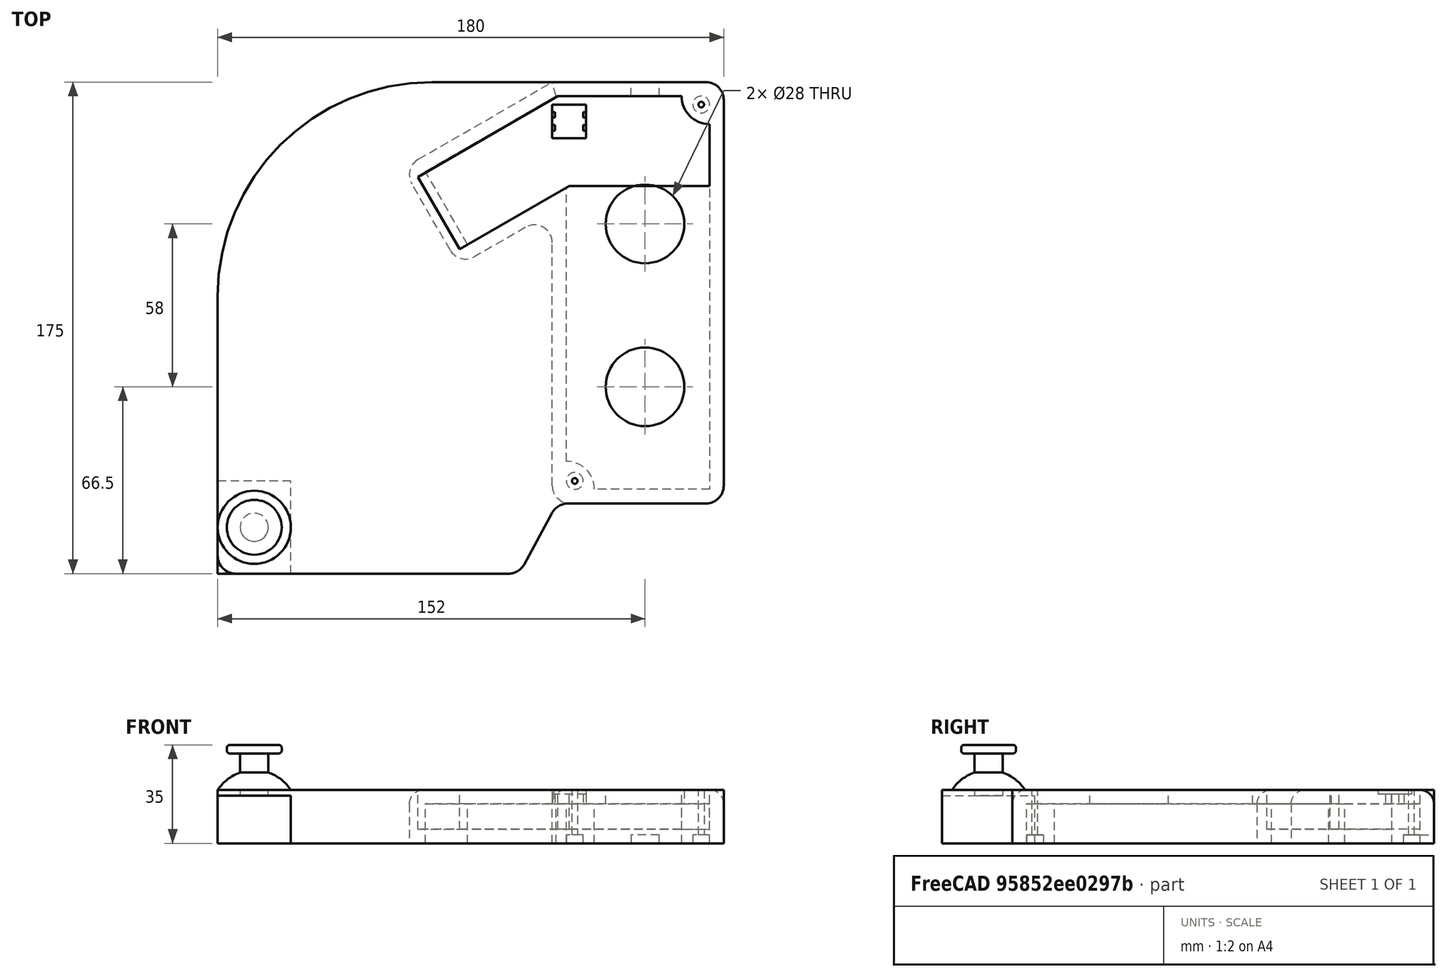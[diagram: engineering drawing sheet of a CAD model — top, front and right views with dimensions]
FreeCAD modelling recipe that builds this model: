
FCSTD DOCUMENT  (FreeCAD 0.19R21125 (Git))
Label: base1
Comment: HyperController Enclosure Prototype
License: GPLv3
LicenseURL: https://www.gnu.org/licenses/gpl-3.0.en.html
objects: Sketcher::SketchObject×17, PartDesign::CoordinateSystem×9, PartDesign::Pocket×8, PartDesign::Pad×5, App::Link×5, PartDesign::Fillet×4, PartDesign::Body×3, App::DocumentObjectGroup×2, App::FeaturePython×2, App::Part×2, PartDesign::Revolution×1, Mesh::Feature×1
note: 65 computed .brp shape members not serialized (recipe doc carries the construction recipe); baked Part::Feature solids carry a one-line shape summary decoded from their .brp

FEATURE [Sketcher::SketchObject] Sketch  label="Base_Ref"
  MapMode = 5
  Support = -> [XY_Plane]
  expr: Constraints[9] = vars.base_l
  expr: Constraints[10] = vars.base_w
  sketch-geometry (4):
    g0: LineSegment StartX=0 StartY=175 StartZ=0 EndX=180 EndY=175 EndZ=0
    g1: LineSegment StartX=180 StartY=175 StartZ=0 EndX=180 EndY=0 EndZ=0
    g2: LineSegment StartX=180 StartY=0 StartZ=0 EndX=0 EndY=0 EndZ=0
    g3: LineSegment StartX=0 StartY=0 StartZ=0 EndX=0 EndY=175 EndZ=0
  constraints (11):
    c: Coincident(g0,g1)
    c: Coincident(g1,g2)
    c: Coincident(g2,g3)
    c: Coincident(g3,g0)
    c: Horizontal(g0)
    c: Horizontal(g2)
    c: Vertical(g1)
    c: Vertical(g3)
    c: Coincident(g2,g-1)
    c: DistanceY(g1,g1) = 175
    c: DistanceX(g0,g0) = 180
FEATURE [Sketcher::SketchObject] Sketch001  label="Base"
  ExternalGeometry = -> [Sketch]
  MapMode = 5
  Support = -> [XY_Plane]
  expr: Constraints[6] = vars.round
  expr: Constraints[10] = vars.round
  expr: Constraints[17] = vars.big_round
  expr: Constraints[22] = vars.round
  expr: Constraints[23] = vars.round
  expr: Constraints[24] = vars.joystick1_margin_out - vars.joystick1_margin_in
  expr: Constraints[25] = vars.joystick1_margin_right + vars.joystick_w + vars.joystick1_margin_left
  sketch-geometry (11):
    g0: LineSegment StartX=180 StartY=175 StartZ=0 EndX=180 EndY=31.35 EndZ=0
    g1: LineSegment StartX=173.65 StartY=25 StartZ=0 EndX=124.577 EndY=25 EndZ=0
    g2: LineSegment StartX=119 StartY=21.6858 StartZ=0 EndX=109 EndY=3.31418 EndZ=0
    g3: LineSegment StartX=103.423 StartY=0 StartZ=0 EndX=6.35 EndY=0 EndZ=0
    g4: ArcOfCircle CenterX=124.577 CenterY=18.65 CenterZ=0 NormalX=0 NormalY=0 NormalZ=1 AngleXU=0 Radius=6.35 StartAngle=1.5708 EndAngle=2.64312
    g5: ArcOfCircle CenterX=103.423 CenterY=6.35 CenterZ=0 NormalX=0 NormalY=0 NormalZ=1 AngleXU=0 Radius=6.35 StartAngle=4.71239 EndAngle=5.78472
    g6: LineSegment StartX=180 StartY=175 StartZ=0 EndX=76.2 EndY=175 EndZ=0
    g7: LineSegment StartX=0 StartY=98.8 StartZ=0 EndX=0 EndY=6.35 EndZ=0
    g8: ArcOfCircle CenterX=76.2 CenterY=98.8 CenterZ=0 NormalX=0 NormalY=0 NormalZ=1 AngleXU=0 Radius=76.2 StartAngle=1.5708 EndAngle=3.14159
    g9: ArcOfCircle CenterX=173.65 CenterY=31.35 CenterZ=0 NormalX=0 NormalY=0 NormalZ=1 AngleXU=0 Radius=6.35 StartAngle=4.71239 EndAngle=6.28319
    g10: ArcOfCircle CenterX=6.35 CenterY=6.35 CenterZ=0 NormalX=0 NormalY=0 NormalZ=1 AngleXU=0 Radius=6.35 StartAngle=3.14159 EndAngle=4.71239
  constraints (27):
    c: Coincident(g-3,g0)
    c: Vertical(g0)
    c: Horizontal(g1)
    c: PointOnObject(g3,g-5)
    c: Tangent(g4,g1) = -1.5708
    c: Tangent(g4,g2) = -1.5708
    c: Radius(g4) = 6.35
    c: PointOnObject(g3,g-5)
    c: Tangent(g5,g2) = 1.5708
    c: Tangent(g5,g3) = 1.5708
    c: Radius(g5) = 6.35
    c: Coincident(g6,g0)
    c: Horizontal(g6)
    c: PointOnObject(g7,g-4)
    c: PointOnObject(g7,g-4)
    c: Tangent(g8,g6) = -1.5708
    c: Tangent(g8,g7) = -1.5708
    c: Radius(g8) = 76.2
    c: Tangent(g9,g0) = 1.5708
    c: Tangent(g9,g1) = 1.5708
    c: Tangent(g10,g3) = 1.5708
    c: Tangent(g10,g7) = -1.5708
    c: Radius(g10) = 6.35
    c: Radius(g9) = 6.35
    c: DistanceY(g-5,g1) = 25
    c: DistanceX(g2,g0) = 61
    c: DistanceX(g2,g2) = 10
FEATURE [PartDesign::Pad] Pad
  Length = 19
  Length2 = 100
  Profile = -> Sketch001
  Type = 0
  expr: Length = vars.base_t
FEATURE [Sketcher::SketchObject] Sketch002  label="Base_Ref001"
  MapMode = 5
  Support = -> [XY_Plane001]
  expr: Constraints[10] = vars.base_w
  expr: Constraints[9] = vars.base_l
  sketch-geometry (4):
    g0: LineSegment StartX=0 StartY=175 StartZ=0 EndX=180 EndY=175 EndZ=0
    g1: LineSegment StartX=180 StartY=175 StartZ=0 EndX=180 EndY=0 EndZ=0
    g2: LineSegment StartX=180 StartY=0 StartZ=0 EndX=0 EndY=0 EndZ=0
    g3: LineSegment StartX=0 StartY=0 StartZ=0 EndX=0 EndY=175 EndZ=0
  constraints (11):
    c: Coincident(g0,g1)
    c: Coincident(g1,g2)
    c: Coincident(g2,g3)
    c: Coincident(g3,g0)
    c: Horizontal(g0)
    c: Horizontal(g2)
    c: Vertical(g1)
    c: Vertical(g3)
    c: Coincident(g2,g-1)
    c: DistanceY(g1,g1) = 175
    c: DistanceX(g0,g0) = 180
FEATURE [Sketcher::SketchObject] Sketch003  label="Base001"
  ExternalGeometry = -> [Sketch002]
  MapMode = 5
  Support = -> [XY_Plane001]
  expr: Constraints[25] = vars.joystick1_margin_right + vars.joystick_w + vars.joystick1_margin_left
  expr: Constraints[24] = vars.joystick1_margin_out - vars.joystick1_margin_in
  expr: Constraints[23] = vars.round
  expr: Constraints[22] = vars.round
  expr: Constraints[17] = vars.big_round
  expr: Constraints[10] = vars.round
  expr: Constraints[6] = vars.round
  sketch-geometry (11):
    g0: LineSegment StartX=180 StartY=175 StartZ=0 EndX=180 EndY=31.35 EndZ=0
    g1: LineSegment StartX=173.65 StartY=25 StartZ=0 EndX=124.577 EndY=25 EndZ=0
    g2: LineSegment StartX=119 StartY=21.6858 StartZ=0 EndX=109 EndY=3.31418 EndZ=0
    g3: LineSegment StartX=103.423 StartY=0 StartZ=0 EndX=6.35 EndY=0 EndZ=0
    g4: ArcOfCircle CenterX=124.577 CenterY=18.65 CenterZ=0 NormalX=0 NormalY=0 NormalZ=1 AngleXU=0 Radius=6.35 StartAngle=1.5708 EndAngle=2.64312
    g5: ArcOfCircle CenterX=103.423 CenterY=6.35 CenterZ=0 NormalX=0 NormalY=0 NormalZ=1 AngleXU=0 Radius=6.35 StartAngle=4.71239 EndAngle=5.78472
    g6: LineSegment StartX=180 StartY=175 StartZ=0 EndX=76.2 EndY=175 EndZ=0
    g7: LineSegment StartX=0 StartY=98.8 StartZ=0 EndX=0 EndY=6.35 EndZ=0
    g8: ArcOfCircle CenterX=76.2 CenterY=98.8 CenterZ=0 NormalX=0 NormalY=0 NormalZ=1 AngleXU=0 Radius=76.2 StartAngle=1.5708 EndAngle=3.14159
    g9: ArcOfCircle CenterX=173.65 CenterY=31.35 CenterZ=0 NormalX=0 NormalY=0 NormalZ=1 AngleXU=0 Radius=6.35 StartAngle=4.71239 EndAngle=6.28319
    g10: ArcOfCircle CenterX=6.35 CenterY=6.35 CenterZ=0 NormalX=0 NormalY=0 NormalZ=1 AngleXU=0 Radius=6.35 StartAngle=3.14159 EndAngle=4.71239
  constraints (27):
    c: Coincident(g-3,g0)
    c: Vertical(g0)
    c: Horizontal(g1)
    c: PointOnObject(g3,g-5)
    c: Tangent(g4,g1) = -1.5708
    c: Tangent(g4,g2) = -1.5708
    c: Radius(g4) = 6.35
    c: PointOnObject(g3,g-5)
    c: Tangent(g5,g2) = 1.5708
    c: Tangent(g5,g3) = 1.5708
    c: Radius(g5) = 6.35
    c: Coincident(g6,g0)
    c: Horizontal(g6)
    c: PointOnObject(g7,g-4)
    c: PointOnObject(g7,g-4)
    c: Tangent(g8,g6) = -1.5708
    c: Tangent(g8,g7) = -1.5708
    c: Radius(g8) = 76.2
    c: Tangent(g9,g0) = 1.5708
    c: Tangent(g9,g1) = 1.5708
    c: Tangent(g10,g3) = 1.5708
    c: Tangent(g10,g7) = -1.5708
    c: Radius(g10) = 6.35
    c: Radius(g9) = 6.35
    c: DistanceY(g-5,g1) = 25
    c: DistanceX(g2,g0) = 61
    c: DistanceX(g2,g2) = 10
FEATURE [Sketcher::SketchObject] Sketch004
  ExternalGeometry = -> [Sketch002]
  MapMode = 5
  Support = -> [XY_Plane001]
  expr: Constraints[18] = vars.joystick_sep
  expr: Constraints[19] = vars.joystick1_margin_right
  expr: Constraints[23] = vars.joystick_w
  expr: Constraints[20] = vars.joystick1_margin_out
  expr: Constraints[22] = vars.joystick_l
  expr: Constraints[25] = vars.joystick_w / 2 + 1
  sketch-geometry (11):
    g0: LineSegment [constr] StartX=139 StartY=83 StartZ=0 EndX=165 EndY=83 EndZ=0
    g1: LineSegment [constr] StartX=165 StartY=83 StartZ=0 EndX=165 EndY=50 EndZ=0
    g2: LineSegment [constr] StartX=165 StartY=50 StartZ=0 EndX=139 EndY=50 EndZ=0
    g3: LineSegment [constr] StartX=139 StartY=50 StartZ=0 EndX=139 EndY=83 EndZ=0
    g4: LineSegment [constr] StartX=139 StartY=141 StartZ=0 EndX=165 EndY=141 EndZ=0
    g5: LineSegment [constr] StartX=165 StartY=141 StartZ=0 EndX=165 EndY=108 EndZ=0
    g6: LineSegment [constr] StartX=165 StartY=108 StartZ=0 EndX=139 EndY=108 EndZ=0
    g7: LineSegment [constr] StartX=139 StartY=108 StartZ=0 EndX=139 EndY=141 EndZ=0
    g8: Circle CenterX=152 CenterY=124.5 CenterZ=0 NormalX=0 NormalY=0 NormalZ=1 AngleXU=0 Radius=14
    g9: GeomPoint X=152 Y=66.5 Z=0
    g10: Circle CenterX=152 CenterY=66.5 CenterZ=0 NormalX=0 NormalY=0 NormalZ=1 AngleXU=0 Radius=14
  constraints (29):
    c: Coincident(g0,g1)
    c: Coincident(g1,g2)
    c: Coincident(g2,g3)
    c: Coincident(g3,g0)
    c: Horizontal(g0)
    c: Horizontal(g2)
    c: Vertical(g1)
    c: Vertical(g3)
    c: Coincident(g4,g5)
    c: Coincident(g5,g6)
    c: Coincident(g6,g7)
    c: Coincident(g7,g4)
    c: Horizontal(g4)
    c: Horizontal(g6)
    c: Vertical(g5)
    c: Vertical(g7)
    c: PointOnObject(g6,g3)
    c: PointOnObject(g5,g1)
    c: DistanceY(g0,g5) = 25
    c: DistanceX(g1,g-3) = 15
    c: DistanceY(g-3,g1) = 50
    c: Equal(g5,g1)
    c: DistanceY(g1,g1) = 33
    c: DistanceX(g4,g4) = 26
    c: Symmetric(g5,g4,g8)
    c: Radius(g8) = 14
    c: Symmetric(g0,g1,g9)
    c: Coincident(g10,g9)
    c: Equal(g10,g8)
FEATURE [PartDesign::CoordinateSystem] LCS_Origin
  AttacherType = Attacher::AttachEngine3D
  MapMode = 2
  Support = -> [X_Axis002]
FEATURE [App::DocumentObjectGroup] Constraints
FEATURE [App::FeaturePython] Variables  # WARN: FeaturePython — macro-defined, semantics opaque (R4)
FEATURE [App::Link] BasePlate  label="BasePlate001"
  LinkedObject = -> Body
FEATURE [PartDesign::CoordinateSystem] LCS_1
  AttacherType = Attacher::AttachEngine3D
  MapMode = 7
  Placement = pos=(180,0,0) rot=(0,0.707107,0.707107;3.14159rad)
  Support = -> [Sketch]
FEATURE [PartDesign::CoordinateSystem] LCS_2
  AttacherType = Attacher::AttachEngine3D
  MapMode = 7
  Placement = pos=(180,0,0) rot=(0,0.707107,0.707107;3.14159rad)
  Support = -> [Sketch002]
FEATURE [App::Link] TopPlate  label="TopPlate001"
  AssemblyType = Asm4EE
  AttachedBy = #LCS_2
  AttachedTo = BasePlate#LCS_1
  AttachmentOffset = pos=(0,19,0) rot=(0,0,1;0rad)
  LinkPlacement = pos=(0,-3.6e-15,19) rot=(0,0,1;0rad)
  LinkedObject = -> Body001
  Placement = pos=(0,-3.6e-15,19) rot=(0,0,1;0rad)
  expr: Placement = BasePlate.Placement * LCS_1.Placement * AttachmentOffset * LCS_2.Placement ^ -1
  expr: .AttachmentOffset.Base.y = vars.base_t
FEATURE [Sketcher::SketchObject] Sketch005
  ExternalGeometry = -> [Sketch002]
  MapMode = 5
  Support = -> [XY_Plane001]
  expr: Constraints[56] = vars.buttons_l
  expr: Constraints[46] = vars.buttons_angle
  expr: Constraints[32] = vars.joystick1_margin_out - vars.joystick1_margin_in
  expr: Constraints[28] = vars.round
  expr: Constraints[55] = vars.buttons_w
  expr: Constraints[22] = vars.joystick_l
  expr: Constraints[20] = vars.joystick1_margin_out
  expr: Constraints[23] = vars.joystick_w
  expr: Constraints[19] = vars.joystick1_margin_right
  expr: Constraints[36] = vars.joystick1_margin_left
  expr: Constraints[18] = vars.joystick_sep
  sketch-geometry (21):
    g0: LineSegment [constr] StartX=139 StartY=83 StartZ=0 EndX=165 EndY=83 EndZ=0
    g1: LineSegment [constr] StartX=165 StartY=83 StartZ=0 EndX=165 EndY=50 EndZ=0
    g2: LineSegment [constr] StartX=165 StartY=50 StartZ=0 EndX=139 EndY=50 EndZ=0
    g3: LineSegment [constr] StartX=139 StartY=50 StartZ=0 EndX=139 EndY=83 EndZ=0
    g4: LineSegment [constr] StartX=139 StartY=141 StartZ=0 EndX=165 EndY=141 EndZ=0
    g5: LineSegment [constr] StartX=165 StartY=141 StartZ=0 EndX=165 EndY=108 EndZ=0
    g6: LineSegment [constr] StartX=165 StartY=108 StartZ=0 EndX=139 EndY=108 EndZ=0
    g7: LineSegment [constr] StartX=139 StartY=108 StartZ=0 EndX=139 EndY=141 EndZ=0
    g8: LineSegment StartX=119 StartY=31.35 StartZ=0 EndX=119 EndY=117.813 EndZ=0
    g9: LineSegment StartX=109.475 StartY=123.313 StartZ=0 EndX=91.3686 EndY=112.859 EndZ=0
    g10: LineSegment StartX=82.6943 StartY=115.183 StartZ=0 EndX=69.0443 EndY=138.826 EndZ=0
    g11: LineSegment StartX=71.3686 StartY=147.5 StartZ=0 EndX=119 EndY=175 EndZ=0
    g12: LineSegment StartX=119 StartY=175 StartZ=0 EndX=173.65 EndY=175 EndZ=0
    g13: LineSegment StartX=180 StartY=168.65 StartZ=0 EndX=180 EndY=31.35 EndZ=0
    g14: LineSegment StartX=173.65 StartY=25 StartZ=0 EndX=125.35 EndY=25 EndZ=0
    g15: ArcOfCircle CenterX=173.65 CenterY=31.35 CenterZ=0 NormalX=0 NormalY=0 NormalZ=1 AngleXU=0 Radius=6.35 StartAngle=4.71239 EndAngle=6.28319
    g16: ArcOfCircle CenterX=125.35 CenterY=31.35 CenterZ=0 NormalX=0 NormalY=0 NormalZ=1 AngleXU=0 Radius=6.35 StartAngle=3.14159 EndAngle=4.71239
    g17: ArcOfCircle CenterX=112.65 CenterY=117.813 CenterZ=0 NormalX=0 NormalY=0 NormalZ=1 AngleXU=0 Radius=6.35 StartAngle=7e-16 EndAngle=2.0944
    g18: ArcOfCircle CenterX=88.1936 CenterY=118.358 CenterZ=0 NormalX=0 NormalY=0 NormalZ=1 AngleXU=0 Radius=6.35 StartAngle=3.66519 EndAngle=5.23599
    g19: ArcOfCircle CenterX=74.5436 CenterY=142.001 CenterZ=0 NormalX=0 NormalY=0 NormalZ=1 AngleXU=0 Radius=6.35 StartAngle=2.0944 EndAngle=3.66519
    g20: ArcOfCircle CenterX=173.65 CenterY=168.65 CenterZ=0 NormalX=0 NormalY=0 NormalZ=1 AngleXU=0 Radius=6.35 StartAngle=3e-16 EndAngle=1.5708
  constraints (57):
    c: Coincident(g0,g1)
    c: Coincident(g1,g2)
    c: Coincident(g2,g3)
    c: Coincident(g3,g0)
    c: Horizontal(g0)
    c: Horizontal(g2)
    c: Vertical(g1)
    c: Vertical(g3)
    c: Coincident(g4,g5)
    c: Coincident(g5,g6)
    c: Coincident(g6,g7)
    c: Coincident(g7,g4)
    c: Horizontal(g4)
    c: Horizontal(g6)
    c: Vertical(g5)
    c: Vertical(g7)
    c: PointOnObject(g6,g3)
    c: PointOnObject(g5,g1)
    c: DistanceY(g0,g5) = 25
    c: DistanceX(g1,g-3) = 15
    c: DistanceY(g-3,g1) = 50
    c: Equal(g5,g1)
    c: DistanceY(g1,g1) = 33
    c: DistanceX(g4,g4) = 26
    c: Vertical(g8)
    c: Horizontal(g12)
    c: Tangent(g15,g13) = 1.5708
    c: Tangent(g15,g14) = 1.5708
    c: Radius(g15) = 6.35
    c: Horizontal(g14)
    c: Vertical(g13)
    c: PointOnObject(g-3,g13)
    c: DistanceY(g-3,g14) = 25
    c: Tangent(g16,g14) = 1.5708
    c: Tangent(g16,g8) = 1.5708
    c: Equal(g16,g15)
    c: DistanceX(g8,g2) = 20
    c: Tangent(g17,g8) = -1.5708
    c: Tangent(g17,g9) = -1.5708
    c: Tangent(g19,g11) = 1.5708
    c: Tangent(g18,g9) = 1.5708
    c: Tangent(g18,g10) = 1.5708
    c: Equal(g16,g17)
    c: Equal(g17,g18)
    c: Equal(g18,g19)
    c: Parallel(g11,g9)
    c: Angle(g9,g8) = 1.0472
    c: Perpendicular(g9,g10)
    c: Tangent(g20,g13) = 1.5708
    c: Tangent(g20,g12) = 1.5708
    c: Equal(g16,g20)
    c: Coincident(g11,g12)
    c: PointOnObject(g11,g8)
    c: PointOnObject(g11,g-4)
    c: Tangent(g10,g19) = 1.5708
    c: Distance(g9,g11) = 40
    c: Distance(g11) = 55
FEATURE [PartDesign::Pad] Pad001
  Length = 19
  Length2 = 100
  Profile = -> Sketch005
  Type = 0
  expr: Length = vars.base_t
FEATURE [PartDesign::Pocket] Pocket
  BaseFeature = -> Pad001
  Length = 5
  Length2 = 100
  Midplane = true
  Profile = -> Sketch004
  Type = 1
FEATURE [Sketcher::SketchObject] Sketch006
  ExternalGeometry = -> [Sketch005]
  MapMode = 5
  Support = -> [XY_Plane001]
  expr: Constraints[11] = vars.top_wall
  expr: Constraints[16] = vars.buttons_w - 2 * vars.top_wall
  expr: Constraints[12] = vars.top_wall
  expr: Constraints[10] = vars.top_wall
  expr: Constraints[32] = vars.top_wall
  sketch-geometry (11):
    g0: LineSegment StartX=73.8686 StartY=143.17 StartZ=0 EndX=120.34 EndY=170 EndZ=0
    g1: LineSegment StartX=120.34 StartY=170 StartZ=0 EndX=165 EndY=170 EndZ=0
    g2: LineSegment StartX=175 StartY=160 StartZ=0 EndX=175 EndY=30 EndZ=0
    g3: LineSegment StartX=175 StartY=30 StartZ=0 EndX=134 EndY=30 EndZ=0
    g4: LineSegment StartX=124 StartY=40 StartZ=0 EndX=124 EndY=137.472 EndZ=0
    g5: LineSegment StartX=124 StartY=137.472 StartZ=0 EndX=88.8686 EndY=117.189 EndZ=0
    g6: LineSegment StartX=88.8686 StartY=117.189 StartZ=0 EndX=73.8686 EndY=143.17 EndZ=0
    g7: LineSegment [constr] StartX=71.3686 StartY=147.5 StartZ=0 EndX=73.8686 EndY=143.17 EndZ=0
    g8: LineSegment [constr] StartX=88.8686 StartY=117.189 StartZ=0 EndX=91.3686 EndY=112.859 EndZ=0
    g9: ArcOfCircle CenterX=175 CenterY=170 CenterZ=0 NormalX=0 NormalY=0 NormalZ=1 AngleXU=0 Radius=10 StartAngle=3.14159 EndAngle=4.71239
    g10: ArcOfCircle CenterX=124 CenterY=30 CenterZ=0 NormalX=0 NormalY=0 NormalZ=1 AngleXU=0 Radius=10 StartAngle=-9e-16 EndAngle=1.5708
  constraints (33):
    c: Coincident(g0,g1)
    c: Horizontal(g1)
    c: Vertical(g2)
    c: Coincident(g2,g3)
    c: Vertical(g4)
    c: Coincident(g4,g5)
    c: Coincident(g5,g6)
    c: Parallel(g-3,g3)
    c: Parallel(g5,g-8)
    c: Parallel(g6,g-9)
    c: DistanceY(g-3,g2) = 5
    c: DistanceX(g2,g-5) = 5
    c: DistanceY(g1,g-6) = 5
    c: Coincident(g0,g6)
    c: Parallel(g0,g-7)
    c: PointOnObject(g-7,g6)
    c: Distance(g6) = 30
    c: Coincident(g7,g-7)
    c: Coincident(g7,g0)
    c: Coincident(g8,g5)
    c: Coincident(g8,g-8)
    c: Equal(g8,g7)
    c: Coincident(g9,g1)
    c: Coincident(g9,g2)
    c: Radius(g9) = 10
    c: PointOnObject(g9,g1)
    c: PointOnObject(g9,g2)
    c: Coincident(g10,g4)
    c: Coincident(g10,g3)
    c: Equal(g9,g10)
    c: PointOnObject(g10,g4)
    c: PointOnObject(g10,g3)
    c: DistanceX(g-4,g10) = 5
FEATURE [PartDesign::Pocket] Pocket001
  BaseFeature = -> Pocket
  Length = 14
  Length2 = 100
  Profile = -> Sketch006
  Reversed = true
  Type = 0
  expr: Length = vars.base_t - vars.top_wall
FEATURE [PartDesign::Fillet] Fillet001
  Base = -> Pad [Edge1]
  BaseFeature = -> Pad
  Radius = 6.35
  SupportTransform = true
  expr: Radius = vars.round
FEATURE [Sketcher::SketchObject] Sketch007
  AttachmentOffset = pos=(0,0,5) rot=(0,0,1;0rad)
  ExternalGeometry = -> [Sketch]
  MapMode = 5
  Placement = pos=(0,0,5) rot=(0,0,1;0rad)
  Support = -> [XY_Plane]
  expr: Constraints[12] = vars.top_wall
  expr: .AttachmentOffset.Base.z = vars.top_wall
  expr: Constraints[11] = vars.top_wall
  expr: Constraints[5] = 22
  expr: Constraints[19] = vars.buttons_angle + 90
  expr: Constraints[20] = 45
  sketch-geometry (7):
    g0: LineSegment StartX=165 StartY=170 StartZ=0 EndX=121 EndY=170 EndZ=0
    g1: LineSegment StartX=125 StartY=138 StartZ=0 EndX=175 EndY=138 EndZ=0
    g2: LineSegment StartX=175 StartY=138 StartZ=0 EndX=175 EndY=160 EndZ=0
    g3: ArcOfCircle CenterX=175 CenterY=170 CenterZ=0 NormalX=0 NormalY=0 NormalZ=1 AngleXU=0 Radius=10 StartAngle=3.14159 EndAngle=4.71239
    g4: LineSegment StartX=121 StartY=170 StartZ=0 EndX=71.1725 EndY=141.232 EndZ=0
    g5: LineSegment StartX=71.1725 StartY=141.232 StartZ=0 EndX=86.0289 EndY=115.5 EndZ=0
    g6: LineSegment StartX=86.0289 StartY=115.5 StartZ=0 EndX=125 EndY=138 EndZ=0
  constraints (22):
    c: Coincident(g1,g2)
    c: Horizontal(g0)
    c: Horizontal(g1)
    c: Vertical(g2)
    c: DistanceX(g1,g1) = 50
    c: DistanceY(g2,g2) = 22
    c: Coincident(g3,g0)
    c: Coincident(g3,g2)
    c: PointOnObject(g3,g0)
    c: PointOnObject(g3,g2)
    c: Radius(g3) = 10
    c: DistanceX(g2,g-3) = 5
    c: DistanceY(g0,g-3) = 5
    c: Coincident(g0,g4)
    c: Coincident(g4,g5)
    c: Coincident(g5,g6)
    c: Coincident(g6,g1)
    c: Parallel(g6,g4)
    c: Perpendicular(g5,g4)
    c: Angle(g4,g0) = 2.61799
    c: Distance(g6) = 45
    c: DistanceX(g0,g0) = 44
FEATURE [PartDesign::Pocket] Pocket002
  BaseFeature = -> Fillet001
  Length = 5
  Length2 = 100
  Profile = -> Sketch007
  Reversed = true
  Type = 1
FEATURE [Sketcher::SketchObject] Sketch008
  MapMode = 5
  Support = -> [XY_Plane003]
  expr: Constraints[9] = vars.joystick_l
  expr: Constraints[10] = vars.joystick_w
  sketch-geometry (4):
    g0: LineSegment StartX=0 StartY=0 StartZ=0 EndX=26 EndY=0 EndZ=0
    g1: LineSegment StartX=26 StartY=0 StartZ=0 EndX=26 EndY=33 EndZ=0
    g2: LineSegment StartX=26 StartY=33 StartZ=0 EndX=0 EndY=33 EndZ=0
    g3: LineSegment StartX=0 StartY=33 StartZ=0 EndX=0 EndY=0 EndZ=0
  constraints (11):
    c: Coincident(g0,g1)
    c: Coincident(g1,g2)
    c: Coincident(g2,g3)
    c: Coincident(g3,g0)
    c: Horizontal(g0)
    c: Horizontal(g2)
    c: Vertical(g1)
    c: Vertical(g3)
    c: Coincident(g0,g-1)
    c: DistanceY(g1,g1) = 33
    c: DistanceX(g0,g0) = 26
FEATURE [PartDesign::Pad] Pad002
  Length = 17
  Length2 = 100
  Profile = -> Sketch008
  Type = 0
  expr: Length = vars.joystick_h1
FEATURE [Sketcher::SketchObject] Sketch009
  MapMode = 5
  Support = -> [XY_Plane003]
  expr: Constraints[0] = vars.joystick_l / 2
  expr: Constraints[1] = vars.joystick_w / 2
  sketch-geometry (1):
    g0: Circle CenterX=13 CenterY=16.5 CenterZ=0 NormalX=0 NormalY=0 NormalZ=1 AngleXU=0 Radius=5
  constraints (3):
    c: DistanceY(g-1,g0) = 16.5
    c: DistanceX(g-1,g0) = 13
    c: Radius(g0) = 5
FEATURE [PartDesign::Pad] Pad003
  BaseFeature = -> Pad002
  Length = 34
  Length2 = 100
  Profile = -> Sketch009
  Type = 0
  expr: Length = vars.joystick_h2 - 1
FEATURE [Sketcher::SketchObject] Sketch010
  AttachmentOffset = pos=(13,2,-16.5) rot=(0,0,1;0rad)
  MapMode = 5
  Placement = pos=(13,16.5,2) rot=(1,0,0;1.5708rad)
  Support = -> [XZ_Plane003]
  expr: .AttachmentOffset.Base.x = vars.joystick_w / 2
  expr: Constraints[5] = vars.joystick_h1
  expr: .AttachmentOffset.Base.z = -vars.joystick_l / 2
  expr: Constraints[7] = vars.joystick_w / 2
  sketch-geometry (3):
    g0: LineSegment StartX=0 StartY=24 StartZ=0 EndX=0 EndY=17 EndZ=0
    g1: LineSegment StartX=0 StartY=17 StartZ=0 EndX=-13 EndY=17 EndZ=0
    g2: ArcOfCircle CenterX=0 CenterY=8.42857 CenterZ=0 NormalX=0 NormalY=0 NormalZ=1 AngleXU=0 Radius=15.5714 StartAngle=1.5708 EndAngle=2.55868
  constraints (10):
    c: Vertical(g0)
    c: Coincident(g1,g0)
    c: Horizontal(g1)
    c: Coincident(g2,g0)
    c: Coincident(g2,g1)
    c: DistanceY(g-1,g0) = 17
    c: PointOnObject(g2,g0)
    c: DistanceX(g1,g1) = 13
    c: DistanceY(g0,g0) = 7
    c: PointOnObject(g0,g-2)
FEATURE [PartDesign::Revolution] Revolution
  Angle = 360
  Axis = (0,-2e-16,1)
  Base = (13,16.5,2)
  BaseFeature = -> Pad003
  Profile = -> Sketch010
  ReferenceAxis = -> Sketch010 [V_Axis]
FEATURE [Sketcher::SketchObject] Sketch011
  AttachmentOffset = pos=(0,0,33.5) rot=(0,0,1;0rad)
  MapMode = 5
  Placement = pos=(0,0,33.5) rot=(0,0,1;0rad)
  Support = -> [XY_Plane003]
  expr: .AttachmentOffset.Base.z = vars.joystick_h2 - 1.5
  expr: Constraints[2] = vars.joystick_w / 2 * 0.75
  expr: Constraints[1] = vars.joystick_w / 2
  expr: Constraints[0] = vars.joystick_l / 2
  sketch-geometry (1):
    g0: Circle CenterX=13 CenterY=16.5 CenterZ=0 NormalX=0 NormalY=0 NormalZ=1 AngleXU=0 Radius=9.75
  constraints (3):
    c: DistanceY(g-1,g0) = 16.5
    c: DistanceX(g-1,g0) = 13
    c: Radius(g0) = 9.75
FEATURE [PartDesign::Pad] Pad004
  BaseFeature = -> Revolution
  Length = 3
  Length2 = 100
  Midplane = true
  Profile = -> Sketch011
  Type = 0
FEATURE [PartDesign::Fillet] Fillet002
  Base = -> Pad004 [Edge25]
  BaseFeature = -> Pad004
  Radius = 1
  SupportTransform = true
FEATURE [PartDesign::Fillet] Fillet003
  Base = -> Fillet002 [Edge3]
  BaseFeature = -> Fillet002
  Radius = 1
  SupportTransform = true
FEATURE [PartDesign::CoordinateSystem] LCS_3
  AttacherType = Attacher::AttachEngine3D
  MapMode = 7
  Placement = pos=(26,0,0) rot=(0,0.707107,0.707107;3.14159rad)
  Support = -> [Sketch008]
FEATURE [App::Link] Joystick  label="Joystick001"
  AssemblyType = Asm4EE
  AttachedBy = #LCS_4
  AttachedTo = TopPlate#LCS_6
  LinkPlacement = pos=(139,50,19) rot=(0,0,1;0rad)
  LinkedObject = -> Body002
  Placement = pos=(139,50,19) rot=(0,0,1;0rad)
  expr: Placement = TopPlate.Placement * LCS_6.Placement * AttachmentOffset * LCS_4.Placement ^ -1
FEATURE [App::Link] Joystick001  label="Joystick002"
  AssemblyType = Asm4EE
  AttachedBy = #LCS_4
  AttachedTo = TopPlate#LCS_8
  LinkPlacement = pos=(139,108,19) rot=(0,0,1;0rad)
  LinkedObject = -> Body002
  Placement = pos=(139,108,19) rot=(0,0,1;0rad)
  expr: Placement = TopPlate.Placement * LCS_8.Placement * AttachmentOffset * LCS_4.Placement ^ -1
FEATURE [App::FeaturePython] vars  # WARN: FeaturePython — macro-defined, semantics opaque (R4)
  File = vars.py
  RealName = vars
  Symbols = base_l | base_t | base_w | big_round | round | buttons_angle | buttons_l | buttons_w | push_size | joystick1_margin_in | joystick1_margin_left | joystick1_margin_out | joystick1_margin_right | joystick1_margin_top | joystick_h1 | joystick_h2 | joystick_l | joystick_sep | joystick_w | top_wall | fillet
  Time = 0
  base_l = 175
  base_t = 19
  base_w = 180
  big_round = 76.2
  buttons_angle = 60
  buttons_l = 55
  buttons_w = 40
  fillet = 5
  joystick1_margin_in = 25
  joystick1_margin_left = 20
  joystick1_margin_out = 50
  joystick1_margin_right = 15
  joystick1_margin_top = 30
  joystick_h1 = 17
  joystick_h2 = 35
  joystick_l = 33
  joystick_sep = 25
  joystick_w = 26
  push_size = 12
  round = 6.35
  top_wall = 5
FEATURE [PartDesign::Fillet] Fillet
  Base = -> Pocket001 [Edge31]
  BaseFeature = -> Pocket001
  Radius = 5
  SupportTransform = true
  expr: Radius = vars.fillet
FEATURE [PartDesign::CoordinateSystem] LCS_6
  AttacherType = Attacher::AttachEngine3D
  MapMode = 11
  Placement = pos=(152,66.5,0) rot=(0,0,1;1.5708rad)
  Support = -> [Sketch004]
FEATURE [PartDesign::CoordinateSystem] LCS_8
  AttacherType = Attacher::AttachEngine3D
  MapMode = 11
  Placement = pos=(152,124.5,0) rot=(0,0,1;1.5708rad)
  Support = -> [Sketch004]
FEATURE [PartDesign::CoordinateSystem] LCS_4
  AttacherType = Attacher::AttachEngine3D
  MapMode = 11
  Placement = pos=(13,16.5,0) rot=(0,0,1;1.5708rad)
  Support = -> [Sketch009]
FEATURE [PartDesign::Body] Body002  label="Joystick"
  Group = -> [Sketch008,Pad002,Sketch009,Pad003,Sketch010,Revolution,Sketch011,Pad004,Fillet002,Fillet003,LCS_3,LCS_4]
  Origin = -> Origin003
  Tip = -> Fillet003
FEATURE [Sketcher::SketchObject] Sketch012
  AttachmentOffset = pos=(0,0,19) rot=(0,0,1;0rad)
  ExternalGeometry = -> [Sketch003]
  MapMode = 5
  Placement = pos=(0,0,19) rot=(0,0,1;0rad)
  Support = -> [XY_Plane001]
  expr: Constraints[9] = vars.push_size
  expr: Constraints[10] = vars.fillet + 3
  expr: Constraints[11] = vars.joystick1_margin_left + vars.joystick_w + vars.joystick1_margin_right - vars.push_size
  expr: .AttachmentOffset.Base.z = vars.base_t
  sketch-geometry (4):
    g0: LineSegment StartX=119 StartY=167 StartZ=0 EndX=131 EndY=167 EndZ=0
    g1: LineSegment StartX=131 StartY=167 StartZ=0 EndX=131 EndY=155 EndZ=0
    g2: LineSegment StartX=131 StartY=155 StartZ=0 EndX=119 EndY=155 EndZ=0
    g3: LineSegment StartX=119 StartY=155 StartZ=0 EndX=119 EndY=167 EndZ=0
  constraints (12):
    c: Coincident(g0,g1)
    c: Coincident(g1,g2)
    c: Coincident(g2,g3)
    c: Coincident(g3,g0)
    c: Horizontal(g0)
    c: Horizontal(g2)
    c: Vertical(g1)
    c: Vertical(g3)
    c: Equal(g0,g3)
    c: DistanceY(g1,g1) = 12
    c: DistanceY(g0,g-4) = 8
    c: DistanceX(g0,g-4) = 49
FEATURE [PartDesign::Pocket] Pocket003
  BaseFeature = -> Fillet
  Length = 3
  Length2 = 100
  Midplane = true
  Profile = -> Sketch012
  Reversed = true
  Type = 0
FEATURE [Sketcher::SketchObject] Sketch013
  AttachmentOffset = pos=(0,0,19) rot=(0,0,1;0rad)
  ExternalGeometry = -> [Sketch012]
  MapMode = 5
  Placement = pos=(0,0,19) rot=(0,0,1;0rad)
  Support = -> [XY_Plane001]
  expr: .AttachmentOffset.Base.z = vars.base_t
  sketch-geometry (19):
    g0: LineSegment StartX=119 StartY=164.333 StartZ=0 EndX=120 EndY=164.333 EndZ=0
    g1: LineSegment StartX=120 StartY=164.333 StartZ=0 EndX=120 EndY=162.333 EndZ=0
    g2: LineSegment StartX=120 StartY=162.333 StartZ=0 EndX=119 EndY=162.333 EndZ=0
    g3: LineSegment StartX=119 StartY=162.333 StartZ=0 EndX=119 EndY=164.333 EndZ=0
    g4: LineSegment StartX=130 StartY=164.333 StartZ=0 EndX=131 EndY=164.333 EndZ=0
    g5: LineSegment StartX=131 StartY=164.333 StartZ=0 EndX=131 EndY=162.333 EndZ=0
    g6: LineSegment StartX=131 StartY=162.333 StartZ=0 EndX=130 EndY=162.333 EndZ=0
    g7: LineSegment StartX=130 StartY=162.333 StartZ=0 EndX=130 EndY=164.333 EndZ=0
    g8: LineSegment StartX=119 StartY=159.667 StartZ=0 EndX=120 EndY=159.667 EndZ=0
    g9: LineSegment StartX=120 StartY=159.667 StartZ=0 EndX=120 EndY=157.667 EndZ=0
    g10: LineSegment StartX=120 StartY=157.667 StartZ=0 EndX=119 EndY=157.667 EndZ=0
    g11: LineSegment StartX=119 StartY=157.667 StartZ=0 EndX=119 EndY=159.667 EndZ=0
    g12: LineSegment StartX=130 StartY=159.667 StartZ=0 EndX=131 EndY=159.667 EndZ=0
    g13: LineSegment StartX=131 StartY=159.667 StartZ=0 EndX=131 EndY=157.667 EndZ=0
    g14: LineSegment StartX=131 StartY=157.667 StartZ=0 EndX=130 EndY=157.667 EndZ=0
    g15: LineSegment StartX=130 StartY=157.667 StartZ=0 EndX=130 EndY=159.667 EndZ=0
    g16: LineSegment [constr] StartX=131 StartY=167 StartZ=0 EndX=131 EndY=164.333 EndZ=0
    g17: LineSegment [constr] StartX=131 StartY=162.333 StartZ=0 EndX=131 EndY=159.667 EndZ=0
    g18: LineSegment [constr] StartX=131 StartY=157.667 StartZ=0 EndX=131 EndY=155 EndZ=0
  constraints (54):
    c: Coincident(g0,g1)
    c: Coincident(g1,g2)
    c: Coincident(g2,g3)
    c: Coincident(g3,g0)
    c: Horizontal(g0)
    c: Horizontal(g2)
    c: Vertical(g1)
    c: Vertical(g3)
    c: Coincident(g4,g5)
    c: Coincident(g5,g6)
    c: Coincident(g6,g7)
    c: Coincident(g7,g4)
    c: Horizontal(g4)
    c: Horizontal(g6)
    c: Vertical(g5)
    c: Vertical(g7)
    c: Coincident(g8,g9)
    c: Coincident(g9,g10)
    c: Coincident(g10,g11)
    c: Coincident(g11,g8)
    c: Horizontal(g8)
    c: Horizontal(g10)
    c: Vertical(g9)
    c: Vertical(g11)
    c: Coincident(g12,g13)
    c: Coincident(g13,g14)
    c: Coincident(g14,g15)
    c: Coincident(g15,g12)
    c: Horizontal(g12)
    c: Horizontal(g14)
    c: Vertical(g13)
    c: Vertical(g15)
    c: Equal(g1,g7)
    c: Equal(g7,g9)
    c: Equal(g9,g15)
    c: Equal(g0,g4)
    c: Equal(g4,g8)
    c: Equal(g8,g12)
    c: PointOnObject(g13,g-4)
    c: PointOnObject(g5,g-4)
    c: PointOnObject(g2,g-6)
    c: PointOnObject(g10,g-6)
    c: PointOnObject(g8,g12)
    c: PointOnObject(g0,g4)
    c: DistanceX(g8,g8) = 1
    c: Coincident(g16,g-4)
    c: Coincident(g16,g4)
    c: Coincident(g17,g5)
    c: Coincident(g17,g12)
    c: Coincident(g18,g13)
    c: Coincident(g18,g-5)
    c: Equal(g16,g17)
    c: Equal(g17,g18)
    c: DistanceY(g1,g1) = 2
FEATURE [PartDesign::Pocket] Pocket004
  BaseFeature = -> Pocket003
  Length = 5
  Length2 = 100
  Midplane = true
  Profile = -> Sketch013
  Type = 1
FEATURE [Mesh::Feature] Arduino_Pro_Micro_Header
  Placement = pos=(-10,-7,0) rot=(0,0,1;0rad)
FEATURE [PartDesign::CoordinateSystem] LCS_5
  AttacherType = Attacher::AttachEngine3D
FEATURE [App::Part] Part  label="Arduino"
  Group = -> [Arduino_Pro_Micro_Header,LCS_5]
  Origin = -> Origin004
FEATURE [PartDesign::CoordinateSystem] LCS_7
  AttacherType = Attacher::AttachEngine3D
  MapMode = 7
  Placement = pos=(86.0289,115.5,5) rot=(0.774597,-0.447214,-0.447214;1.82348rad)
  Support = -> [Sketch007]
FEATURE [App::Link] Arduino  label="Arduino001"
  AssemblyType = Asm4EE
  AttachedBy = #LCS_5
  AttachedTo = BasePlate#LCS_7
  AttachmentOffset = pos=(-24,6,-47) rot=(-0.57735,-0.57735,-0.57735;2.0944rad)
  LinkPlacement = pos=(114.732,159.785,11) rot=(0,0,-1;2.61799rad)
  LinkedObject = -> Part
  Placement = pos=(114.732,159.785,11) rot=(0,0,-1;2.61799rad)
  expr: Placement = BasePlate.Placement * LCS_7.Placement * AttachmentOffset * LCS_5.Placement ^ -1
FEATURE [App::Part] Model
  Configuration = 0
  Group = -> [LCS_Origin,Constraints,Variables,BasePlate,TopPlate,Joystick,Joystick001,Arduino]
  Origin = -> Origin002
  Type = Assembly4 Model
FEATURE [Sketcher::SketchObject] Sketch014
  ExternalGeometry = -> [Sketch001]
  MapMode = 5
  Support = -> [XY_Plane]
  sketch-geometry (2):
    g0: Circle CenterX=172 CenterY=167 CenterZ=0 NormalX=0 NormalY=0 NormalZ=1 AngleXU=0 Radius=1
    g1: Circle CenterX=127 CenterY=33 CenterZ=0 NormalX=0 NormalY=0 NormalZ=1 AngleXU=0 Radius=1
  constraints (6):
    c: DistanceY(g0,g-4) = 8
    c: DistanceX(g0,g-4) = 8
    c: Radius(g0) = 1
    c: DistanceY(g-5,g1) = 8
    c: DistanceX(g-6,g1) = 8
    c: Equal(g1,g0)
FEATURE [PartDesign::Pocket] Pocket005
  BaseFeature = -> Pocket002
  Length = 5
  Length2 = 100
  Midplane = true
  Profile = -> Sketch014
  Type = 1
FEATURE [Sketcher::SketchObject] Sketch015
  ExternalGeometry = -> [Sketch014]
  MapMode = 5
  Support = -> [XY_Plane]
  sketch-geometry (2):
    g0: Circle CenterX=127 CenterY=33 CenterZ=0 NormalX=0 NormalY=0 NormalZ=1 AngleXU=0 Radius=3
    g1: Circle CenterX=172 CenterY=167 CenterZ=0 NormalX=0 NormalY=0 NormalZ=1 AngleXU=0 Radius=3
  constraints (4):
    c: Coincident(g-4,g0)
    c: Coincident(g1,g-3)
    c: Equal(g1,g0)
    c: Radius(g1) = 3
FEATURE [PartDesign::Pocket] Pocket006
  BaseFeature = -> Pocket005
  Length = 3
  Length2 = 100
  Profile = -> Sketch015
  Reversed = true
  Type = 0
FEATURE [PartDesign::Body] Body  label="BasePlate"
  Group = -> [Sketch,Sketch001,Pad,LCS_1,Fillet001,Sketch007,Pocket002,LCS_7,Sketch014,Pocket005,Sketch015,Pocket006]
  Origin = -> Origin
  Tip = -> Pocket006
FEATURE [Sketcher::SketchObject] Sketch016
  AttachmentOffset = pos=(0,0,-100) rot=(0,0,1;0rad)
  MapMode = 5
  Placement = pos=(0,100,2.22e-14) rot=(1,0,0;1.5708rad)
  Support = -> [XZ_Plane001]
  sketch-geometry (4):
    g0: LineSegment StartX=147 StartY=3 StartZ=0 EndX=157 EndY=3 EndZ=0
    g1: LineSegment StartX=157 StartY=3 StartZ=0 EndX=157 EndY=0 EndZ=0
    g2: LineSegment StartX=157 StartY=0 StartZ=0 EndX=147 EndY=0 EndZ=0
    g3: LineSegment StartX=147 StartY=0 StartZ=0 EndX=147 EndY=3 EndZ=0
  constraints (12):
    c: Coincident(g0,g1)
    c: Coincident(g1,g2)
    c: Coincident(g2,g3)
    c: Coincident(g3,g0)
    c: Horizontal(g0)
    c: Horizontal(g2)
    c: Vertical(g1)
    c: Vertical(g3)
    c: PointOnObject(g2,g-1)
    c: DistanceY(g1,g1) = 3
    c: DistanceX(g0,g0) = 10
    c: DistanceX(g-1,g2) = 147
FEATURE [PartDesign::Pocket] Pocket007
  BaseFeature = -> Pocket004
  Length = 5
  Length2 = 100
  Profile = -> Sketch016
  Type = 1
FEATURE [PartDesign::Body] Body001  label="TopPlate"
  Group = -> [Sketch002,Sketch003,Sketch004,LCS_2,Sketch005,Pad001,Pocket,Sketch006,Pocket001,Fillet,LCS_6,LCS_8,Sketch012,Pocket003,Sketch013,Pocket004,Sketch016,Pocket007]
  Origin = -> Origin001
  Tip = -> Pocket007
FEATURE [App::DocumentObjectGroup] Parts
  Group = -> [Body,Body001,Body002,Part]
